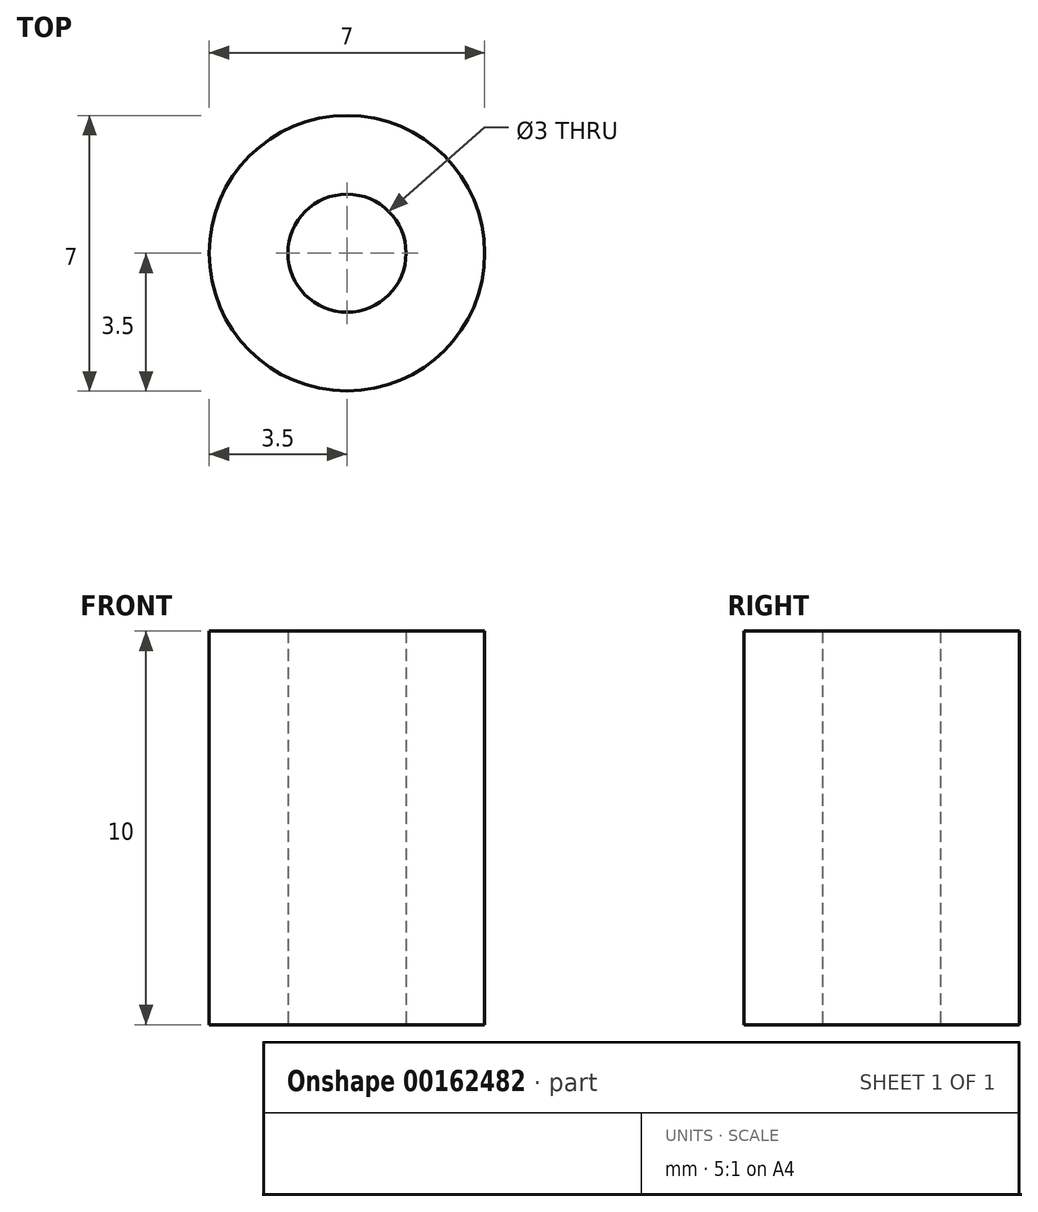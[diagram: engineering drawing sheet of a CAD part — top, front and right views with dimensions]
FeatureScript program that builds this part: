
annotation { "Feature Type Name" : "Feature", "Feature Type Description" : "" }
export const myFeature = defineFeature(function(context is Context, id is Id, definition is map)
    precondition{}
    {
        {
            var Q0;
            Q0=qCreatedBy(makeId("Top.planeOp"),FACE);
            var sketch = newSketch(context, id + "F0", { "sketchPlane" : qUnion([Q0])});
            skCircle(sketch, "E0", {"center": v(0, 0) * mm, "radius": 1.5 * mm});
            skCircle(sketch, "E1", {"center": v(0, 0) * mm, "radius": 3.5 * mm});
            skSolve(sketch);
        }
        {
            var Q0;
            Q0 = qSketchRegion(id + "F0", true);
            extrude(context, id + "F1", {"entities" : qUnion([Q0]), "depth" : 10 * mm});
        }
    });
